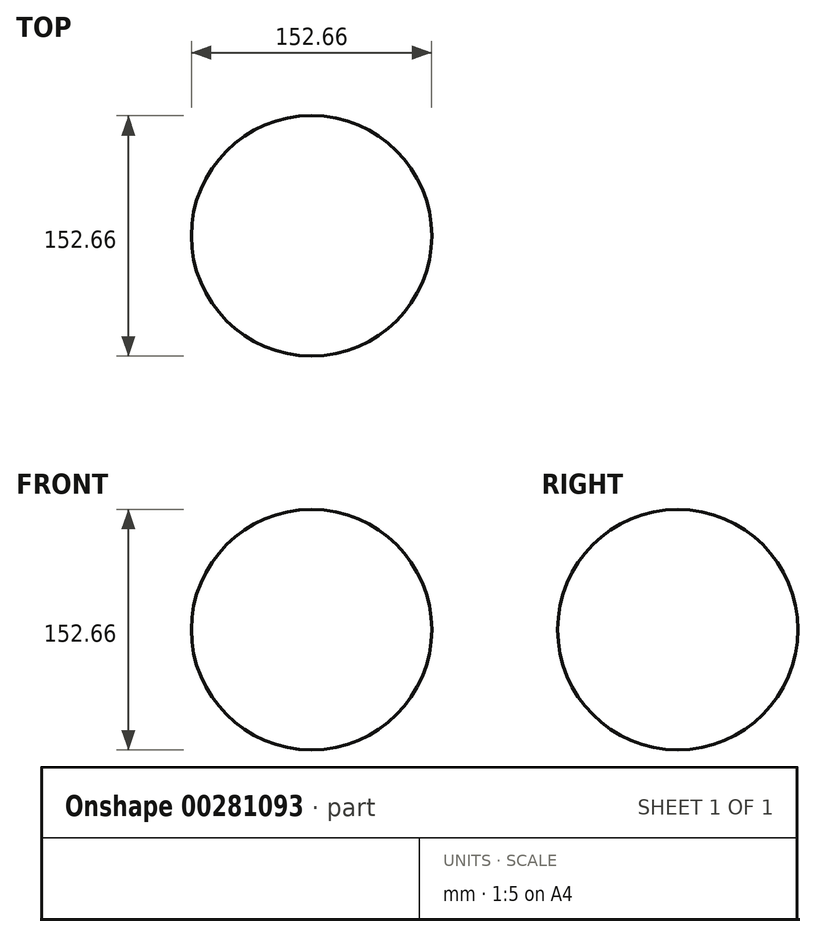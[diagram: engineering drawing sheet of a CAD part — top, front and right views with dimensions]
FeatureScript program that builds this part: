
annotation { "Feature Type Name" : "Feature", "Feature Type Description" : "" }
export const myFeature = defineFeature(function(context is Context, id is Id, definition is map)
    precondition{}
    {
        {
            var Q0;
            Q0=qCreatedBy(makeId("Front.planeOp"),FACE);
            var sketch = newSketch(context, id + "F0", { "sketchPlane" : qUnion([Q0])});
            skLineSegment(sketch, "E0", {"start": v(0, -101.54) * mm, "end": v(0, 98) * mm, "construction": true});
            skArc(sketch, "E1", {"start": v(0, 76.33) * mm, "mid": v(-76.33, 0) * mm, "end": v(0, -76.33) * mm});
            skLineSegment(sketch, "E2", {"start": v(0, 76.33) * mm, "end": v(0, -76.33) * mm});
            skSolve(sketch);
        }
        {
            var Q0;
            Q0=makeQuery(id+"F0.imprint","IMPRINT",FACE,{"disambiguationData":[TD([[makeQuery(id+"F0.imprint","IMPRINT",EDGE,{"derivedFrom":sQuery(id+"F0.wireOp",EDGE,"E1")}),1.0]])]});
            var Q1;
            Q1=sQuery(id+"F0.wireOp",EDGE,"E2");
            revolve(context, id + "F1", {"entities" : qUnion([Q0]), "axis" : qUnion([Q1]), "revolveType" : RevolveType.FULL});
        }
    });
